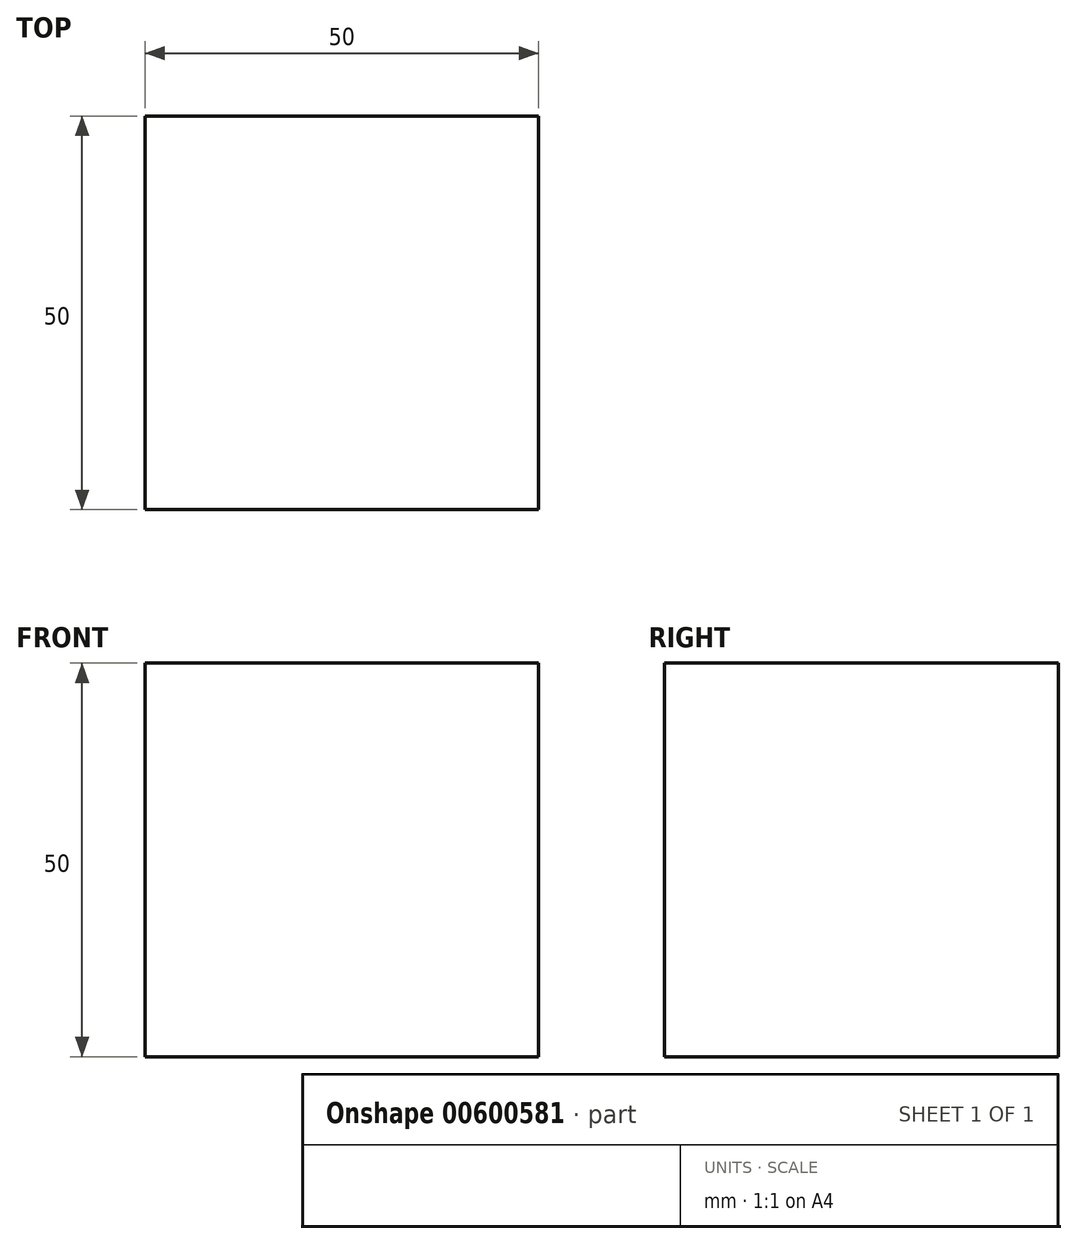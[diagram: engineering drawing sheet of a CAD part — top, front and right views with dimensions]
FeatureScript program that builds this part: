
annotation { "Feature Type Name" : "Feature", "Feature Type Description" : "" }
export const myFeature = defineFeature(function(context is Context, id is Id, definition is map)
    precondition{}
    {
        {
            var Q0;
            Q0=qCreatedBy(makeId("Top.planeOp"),FACE);
            var sketch = newSketch(context, id + "F0", { "sketchPlane" : qUnion([Q0])});
            skLineSegment(sketch, "E0.bottom", {"start": v(-25, 25) * mm, "end": v(25, 25) * mm});
            skLineSegment(sketch, "E0.top", {"start": v(-25, -25) * mm, "end": v(25, -25) * mm});
            skLineSegment(sketch, "E0.left", {"start": v(-25, 25) * mm, "end": v(-25, -25) * mm});
            skLineSegment(sketch, "E0.right", {"start": v(25, 25) * mm, "end": v(25, -25) * mm});
            skPoint(sketch, "E0.middle", {"position": v(0, 0) * mm});
            skSolve(sketch);
        }
        {
            var Q0;
            Q0=makeQuery(id+"F0.imprint","IMPRINT",FACE,{"disambiguationData":[TD([[makeQuery(id+"F0.imprint","IMPRINT",EDGE,{"derivedFrom":sQuery(id+"F0.wireOp",EDGE,"E0.bottom")}),-1.0]])]});
            extrude(context, id + "F1", {"entities" : qUnion([Q0]), "endBound" : BoundingType.SYMMETRIC, "depth" : 50 * mm, "offsetDistance" : 25 * mm});
        }
    });
